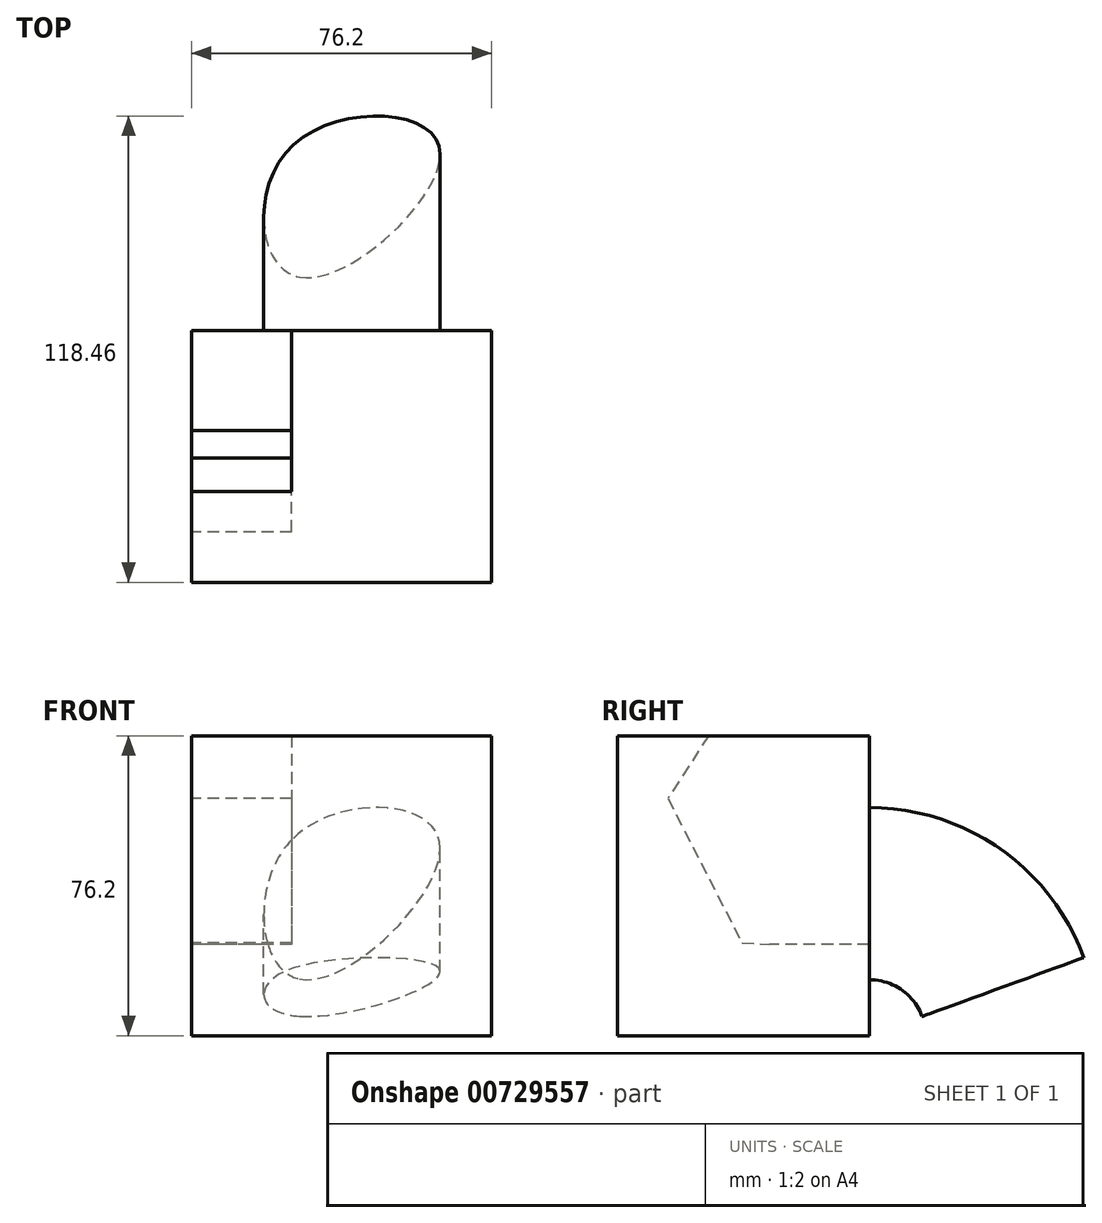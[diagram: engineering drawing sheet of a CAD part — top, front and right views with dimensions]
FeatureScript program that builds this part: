
annotation { "Feature Type Name" : "Feature", "Feature Type Description" : "" }
export const myFeature = defineFeature(function(context is Context, id is Id, definition is map)
    precondition{}
    {
        {
            var Q0;
            Q0=qCreatedBy(makeId("Front.planeOp"),FACE);
            var sketch = newSketch(context, id + "F0", { "sketchPlane" : qUnion([Q0])});
            skLineSegment(sketch, "E0", {"start": v(0, 76.2) * mm, "end": v(0, 0) * mm});
            skLineSegment(sketch, "E1", {"start": v(0, 76.2) * mm, "end": v(-76.2, 76.2) * mm});
            skLineSegment(sketch, "E2", {"start": v(-76.2, 76.2) * mm, "end": v(-76.2, 0) * mm});
            skLineSegment(sketch, "E3", {"start": v(-76.2, 0) * mm, "end": v(0, 0) * mm});
            skSolve(sketch);
        }
        {
            var Q0;
            Q0 = qSketchRegion(id + "F0", true);
            extrude(context, id + "F1", {"entities" : qUnion([Q0]), "oppositeDirection" : true, "depth" : 38.6 * mm, "offsetDistance" : 25.4 * mm});
        }
        {
            var Q0;
            Q0=makeQuery(id+"F1.opExtrude","SWEPT_FACE",FACE,{"disambiguationData":[OSD([sQuery(id+"F0.wireOp",EDGE,"E2")])]});
            var sketch = newSketch(context, id + "F2", { "sketchPlane" : qUnion([Q0])});
            skCircle(sketch, "E4.cCircle", {"center": v(-53.95, 58.21) * mm, "radius": 41.19 * mm, "construction": true});
            skLineSegment(sketch, "E4.0", {"start": v(-72.76, 21.57) * mm, "end": v(-95.1, 56.18) * mm});
            skLineSegment(sketch, "E4.1", {"start": v(-95.1, 56.18) * mm, "end": v(-76.28, 92.82) * mm});
            skLineSegment(sketch, "E4.2", {"start": v(-76.28, 92.82) * mm, "end": v(-35.14, 94.85) * mm});
            skLineSegment(sketch, "E4.3", {"start": v(-35.14, 94.85) * mm, "end": v(-12.81, 60.24) * mm});
            skLineSegment(sketch, "E4.4", {"start": v(-12.81, 60.24) * mm, "end": v(-31.62, 23.6) * mm});
            skLineSegment(sketch, "E4.5", {"start": v(-31.62, 23.6) * mm, "end": v(-72.76, 21.57) * mm});
            skSolve(sketch);
        }
        {
            var Q0;
            Q0 = qSketchRegion(id + "F2", true);
            extrude(context, id + "F3", {"entities" : qUnion([Q0]), "operationType" : NewBodyOperationType.REMOVE, "oppositeDirection" : true, "depth" : 25.4 * mm, "offsetDistance" : 25.4 * mm});
        }
        {
            var Q0;
            Q0=makeQuery(id+"F1.opExtrude","CAP_FACE",FACE,{"disambiguationData":[OSD([sQuery(id+"F0.wireOp",EDGE,"E0"),sQuery(id+"F0.wireOp",EDGE,"E1"),sQuery(id+"F0.wireOp",EDGE,"E2"),sQuery(id+"F0.wireOp",EDGE,"E3")])],"isStart":false});
            extrude(context, id + "F4", {"entities" : qUnion([Q0]), "operationType" : NewBodyOperationType.ADD, "depth" : 25.4 * mm, "offsetDistance" : 25.4 * mm});
        }
        {
            var Q0;
            Q0=makeQuery(id+"F4.opExtrude","CAP_FACE",FACE,{"disambiguationData":[OSD([sQuery(id+"F0.wireOp",EDGE,"E0"),sQuery(id+"F0.wireOp",EDGE,"E1"),sQuery(id+"F0.wireOp",EDGE,"E2"),sQuery(id+"F0.wireOp",EDGE,"E3")])],"isStart":false});
            var sketch = newSketch(context, id + "F5", { "sketchPlane" : qUnion([Q0])});
            skPoint(sketch, "E5.1.internal.snap0", {"position": v(50.8, 49.73) * mm});
            skFitSpline(sketch, "E5", {"points": [v(48.78, 14.4) * mm, v(13.32, 49.73) * mm, v(50.8, 49.73) * mm, v(48.78, 14.4) * mm]});
            skSolve(sketch);
        }
        {
            var Q0;
            Q0 = qSketchRegion(id + "F5", true);
            var Q1;
            Q1=makeQuery(id+"F4.opExtrude","CAP_EDGE",EDGE,{"disambiguationData":[OSD([sQuery(id+"F0.wireOp",EDGE,"E3")])],"isStart":false});
            revolve(context, id + "F6", {"operationType" : NewBodyOperationType.ADD, "surfaceOperationType" : NewSurfaceOperationType.NEW, "entities" : qUnion([Q0]), "axis" : qUnion([Q1]), "revolveType" : RevolveType.ONE_DIRECTION, "oppositeDirection" : true, "angle" : 70 * degree});
        }
    });
